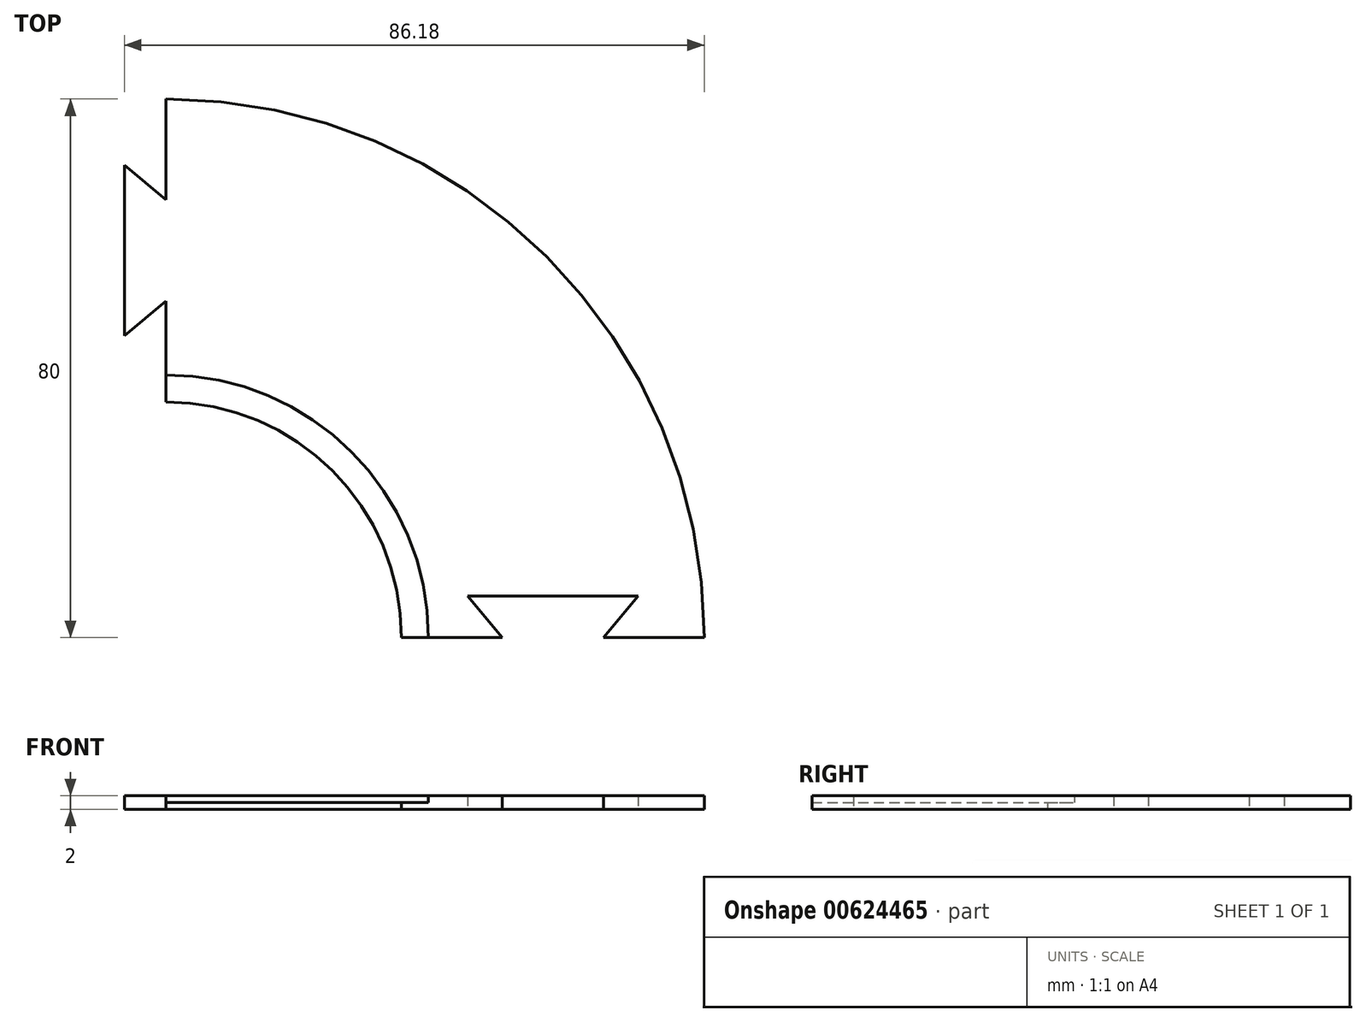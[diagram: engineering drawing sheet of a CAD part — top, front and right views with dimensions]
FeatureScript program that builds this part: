
annotation { "Feature Type Name" : "Feature", "Feature Type Description" : "" }
export const myFeature = defineFeature(function(context is Context, id is Id, definition is map)
    precondition{}
    {
        {
            var Q0;
            Q0=qCreatedBy(makeId("Top.planeOp"),FACE);
            var sketch = newSketch(context, id + "F0", { "sketchPlane" : qUnion([Q0])});
            skArc(sketch, "E0.0", {"start": v(80, 0) * mm, "mid": v(56.57, 56.57) * mm, "end": v(0, 80) * mm});
            skLineSegment(sketch, "E1.0", {"start": v(44.81, 6.18) * mm, "end": v(70.19, 6.18) * mm});
            skLineSegment(sketch, "E2.0", {"start": v(65, 0) * mm, "end": v(80, 0) * mm});
            skArc(sketch, "E3.0", {"start": v(35, 0) * mm, "mid": v(24.75, 24.75) * mm, "end": v(0, 35) * mm});
            skLineSegment(sketch, "E3.1", {"start": v(50, 0) * mm, "end": v(44.81, 6.18) * mm});
            skLineSegment(sketch, "E3.2", {"start": v(70.19, 6.18) * mm, "end": v(65, 0) * mm});
            skLineSegment(sketch, "E4", {"start": v(0, 35) * mm, "end": v(0, 50) * mm});
            skLineSegment(sketch, "E5", {"start": v(0, 65) * mm, "end": v(0, 80) * mm});
            skLineSegment(sketch, "E6", {"start": v(0, 50) * mm, "end": v(-6.18, 44.81) * mm});
            skLineSegment(sketch, "E7", {"start": v(-6.18, 44.81) * mm, "end": v(-6.18, 70.19) * mm});
            skLineSegment(sketch, "E8", {"start": v(-6.18, 70.19) * mm, "end": v(0, 65) * mm});
            skLineSegment(sketch, "E9", {"start": v(50, 0) * mm, "end": v(35, 0) * mm});
            skArc(sketch, "E10.0", {"start": v(39, 0) * mm, "mid": v(27.58, 27.58) * mm, "end": v(0, 39) * mm});
            skSolve(sketch);
        }
        {
            var Q0;
            Q0=makeQuery(id+"F0.imprint","IMPRINT",FACE,{"disambiguationData":[TD([[makeQuery(id+"F0.imprint","IMPRINT",EDGE,{"derivedFrom":sQuery(id+"F0.wireOp",EDGE,"E0.0")}),1.0]])]});
            extrude(context, id + "F1", {"entities" : qUnion([Q0]), "depth" : 2 * mm, "offsetDistance" : 25 * mm});
        }
        {
            var Q0;
            {var subQ0=sQuery(id+"F0.wireOp",EDGE,"E3.0");Q0=makeQuery(id+"F0.imprint","IMPRINT",FACE,{"disambiguationData":[TD([[makeQuery(id+"F0.imprint","IMPRINT",EDGE,{"derivedFrom":subQ0}),-1.0]])]});}
            extrude(context, id + "F2", {"entities" : qUnion([Q0]), "operationType" : NewBodyOperationType.ADD, "depth" : 1 * mm, "offsetDistance" : 25 * mm});
        }
    });
